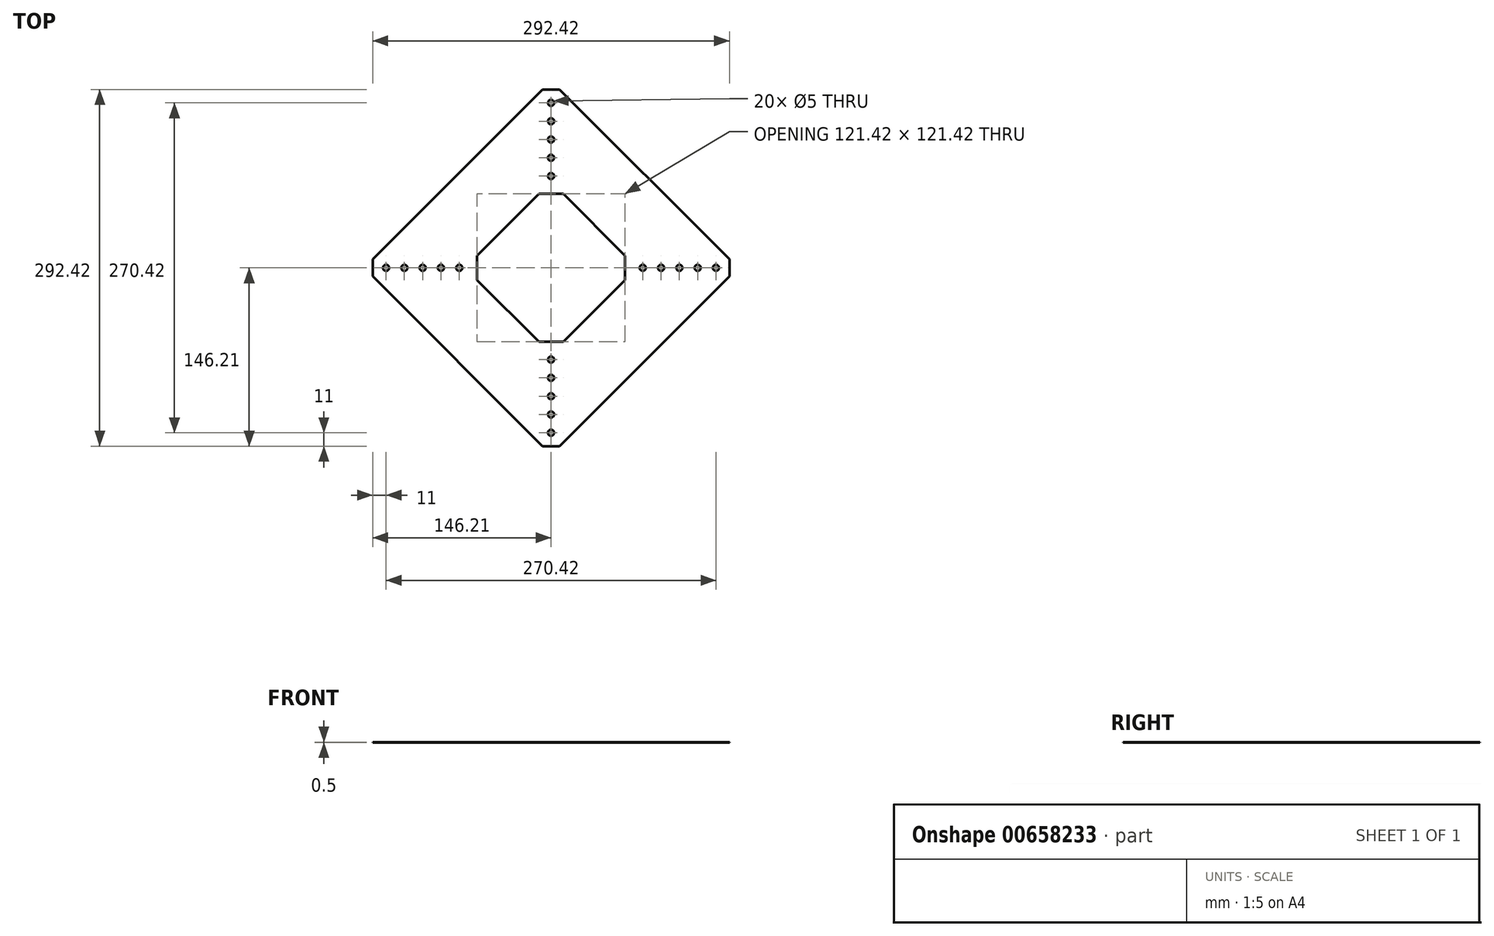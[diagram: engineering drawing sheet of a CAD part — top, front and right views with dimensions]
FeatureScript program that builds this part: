
annotation { "Feature Type Name" : "Feature", "Feature Type Description" : "" }
export const myFeature = defineFeature(function(context is Context, id is Id, definition is map)
    precondition{}
    {
        {
            var Q0;
            Q0=qCreatedBy(makeId("Top.planeOp"),FACE);
            var sketch = newSketch(context, id + "F0", { "sketchPlane" : qUnion([Q0])});
            skPoint(sketch, "E0.center", {"position": v(0, 0) * mm});
            skLineSegment(sketch, "E1", {"start": v(60.7, -10) * mm, "end": v(10, -60.7) * mm});
            skLineSegment(sketch, "E2", {"start": v(-10, -60.7) * mm, "end": v(-60.7, -10) * mm});
            skLineSegment(sketch, "E3", {"start": v(-60.7, 10) * mm, "end": v(-10, 60.7) * mm});
            skLineSegment(sketch, "E4", {"start": v(-10, 60.7) * mm, "end": v(10, 60.7) * mm});
            skLineSegment(sketch, "E5.1.0", {"start": v(-60.7, -10) * mm, "end": v(-60.7, 10) * mm});
            skLineSegment(sketch, "E5.2.0", {"start": v(10, -60.7) * mm, "end": v(-10, -60.7) * mm});
            skLineSegment(sketch, "E5.3.0", {"start": v(60.7, 10) * mm, "end": v(60.7, -10) * mm});
            skLineSegment(sketch, "E6.trimOffspring", {"start": v(10, 60.7) * mm, "end": v(60.71, 10) * mm});
            skLineSegment(sketch, "E7.0", {"start": v(7, -146.21) * mm, "end": v(-7, -146.21) * mm});
            skLineSegment(sketch, "E8.1.0", {"start": v(146.21, 7) * mm, "end": v(146.21, -7) * mm});
            skLineSegment(sketch, "E8.2.0", {"start": v(-7, 146.21) * mm, "end": v(7, 146.21) * mm});
            skLineSegment(sketch, "E8.3.0", {"start": v(-146.21, -7) * mm, "end": v(-146.21, 7) * mm});
            skLineSegment(sketch, "E9", {"start": v(-7, -146.21) * mm, "end": v(-146.21, -7) * mm});
            skLineSegment(sketch, "E10", {"start": v(-146.21, 7) * mm, "end": v(-7, 146.21) * mm});
            skLineSegment(sketch, "E11", {"start": v(7, 146.21) * mm, "end": v(146.21, 7) * mm});
            skLineSegment(sketch, "E12", {"start": v(146.21, -7) * mm, "end": v(7, -146.21) * mm});
            skCircle(sketch, "E13", {"center": v(0, -135.21) * mm, "radius": 2.5 * mm});
            skCircle(sketch, "E14.0.1.0", {"center": v(0, -120.2) * mm, "radius": 2.5 * mm});
            skCircle(sketch, "E14.0.2.0", {"center": v(0, -105.2) * mm, "radius": 2.5 * mm});
            skCircle(sketch, "E14.0.3.0", {"center": v(0, -90.2) * mm, "radius": 2.5 * mm});
            skCircle(sketch, "E14.0.4.0", {"center": v(0, -75.2) * mm, "radius": 2.5 * mm});
            skCircle(sketch, "E15.1.0", {"center": v(75.2, 0) * mm, "radius": 2.5 * mm});
            skCircle(sketch, "E15.1.1", {"center": v(105.2, 0) * mm, "radius": 2.5 * mm});
            skCircle(sketch, "E15.1.2", {"center": v(120.2, 0) * mm, "radius": 2.5 * mm});
            skCircle(sketch, "E15.1.3", {"center": v(90.2, 0) * mm, "radius": 2.5 * mm});
            skCircle(sketch, "E15.1.4", {"center": v(135.21, 0) * mm, "radius": 2.5 * mm});
            skCircle(sketch, "E15.2.0", {"center": v(0, 75.2) * mm, "radius": 2.5 * mm});
            skCircle(sketch, "E15.2.1", {"center": v(0, 105.2) * mm, "radius": 2.5 * mm});
            skCircle(sketch, "E15.2.2", {"center": v(0, 120.2) * mm, "radius": 2.5 * mm});
            skCircle(sketch, "E15.2.3", {"center": v(0, 90.2) * mm, "radius": 2.5 * mm});
            skCircle(sketch, "E15.2.4", {"center": v(0, 135.21) * mm, "radius": 2.5 * mm});
            skCircle(sketch, "E15.3.0", {"center": v(-75.2, 0) * mm, "radius": 2.5 * mm});
            skCircle(sketch, "E15.3.1", {"center": v(-105.2, 0) * mm, "radius": 2.5 * mm});
            skCircle(sketch, "E15.3.2", {"center": v(-120.2, 0) * mm, "radius": 2.5 * mm});
            skCircle(sketch, "E15.3.3", {"center": v(-90.2, 0) * mm, "radius": 2.5 * mm});
            skCircle(sketch, "E15.3.4", {"center": v(-135.21, 0) * mm, "radius": 2.5 * mm});
            skSolve(sketch);
        }
        {
            var Q0;
            Q0=makeQuery(id+"F0.imprint","IMPRINT",FACE,{"disambiguationData":[TD([[makeQuery(id+"F0.imprint","IMPRINT",EDGE,{"derivedFrom":sQuery(id+"F0.wireOp",EDGE,"E1")}),1.0]])]});
            extrude(context, id + "F1", {"entities" : qUnion([Q0]), "depth" : 0.5 * mm, "offsetDistance" : 25 * mm});
        }
    });
